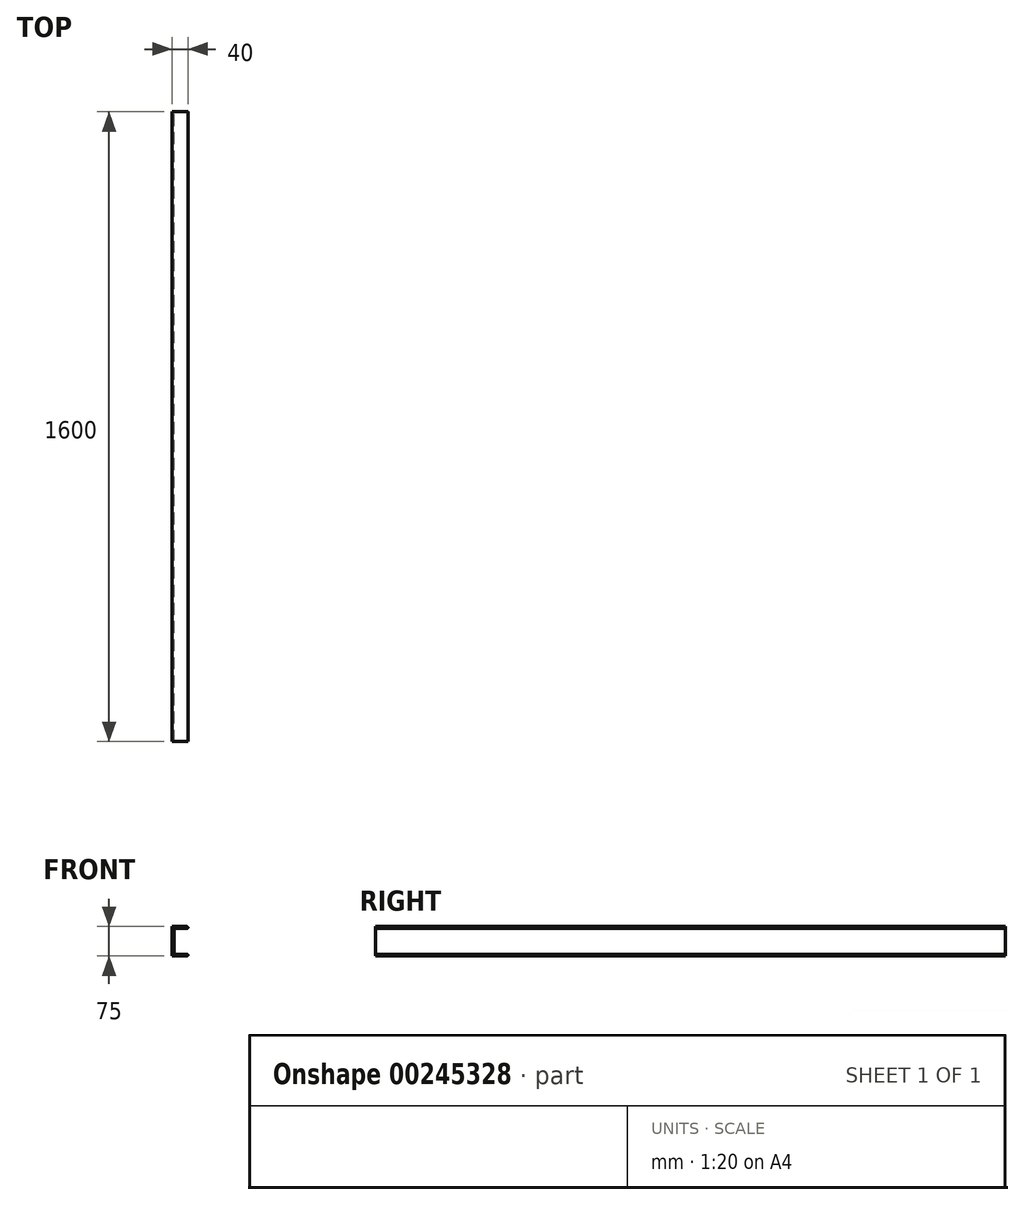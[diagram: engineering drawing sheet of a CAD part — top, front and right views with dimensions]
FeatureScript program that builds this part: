
annotation { "Feature Type Name" : "Feature", "Feature Type Description" : "" }
export const myFeature = defineFeature(function(context is Context, id is Id, definition is map)
    precondition{}
    {
        {
            var Q0;
            Q0=qCreatedBy(makeId("Front.planeOp"),FACE);
            var sketch = newSketch(context, id + "F0", { "sketchPlane" : qUnion([Q0])});
            skLineSegment(sketch, "E0", {"start": v(0, 0) * mm, "end": v(37.5, 0) * mm});
            skLineSegment(sketch, "E1", {"start": v(40, 2.5) * mm, "end": v(40, 2.5) * mm});
            skLineSegment(sketch, "E2", {"start": v(37.5, 5) * mm, "end": v(5, 5) * mm});
            skLineSegment(sketch, "E3", {"start": v(5, 5) * mm, "end": v(5, 70) * mm});
            skLineSegment(sketch, "E4", {"start": v(5, 70) * mm, "end": v(37.5, 70) * mm});
            skLineSegment(sketch, "E5", {"start": v(40, 72.5) * mm, "end": v(40, 72.5) * mm});
            skLineSegment(sketch, "E6", {"start": v(37.5, 75) * mm, "end": v(0, 75) * mm});
            skLineSegment(sketch, "E7", {"start": v(0, 75) * mm, "end": v(0, 0) * mm});
            skPoint(sketch, "E8.visualSharp", {"position": v(40, 75) * mm});
            skArc(sketch, "E8.filletArc", {"start": v(40, 72.5) * mm, "mid": v(39.27, 74.27) * mm, "end": v(37.5, 75) * mm});
            skPoint(sketch, "E9.visualSharp", {"position": v(40, 70) * mm});
            skArc(sketch, "E9.filletArc", {"start": v(37.5, 70) * mm, "mid": v(39.27, 70.73) * mm, "end": v(40, 72.5) * mm});
            skPoint(sketch, "E10.visualSharp", {"position": v(40, 5) * mm});
            skArc(sketch, "E10.filletArc", {"start": v(40, 2.5) * mm, "mid": v(39.27, 4.27) * mm, "end": v(37.5, 5) * mm});
            skPoint(sketch, "E11.visualSharp", {"position": v(40, 0) * mm});
            skArc(sketch, "E11.filletArc", {"start": v(37.5, 0) * mm, "mid": v(39.27, 0.73) * mm, "end": v(40, 2.5) * mm});
            skSolve(sketch);
        }
        {
            var Q0;
            Q0=qSketchRegion(id+"F0",true);
            extrude(context, id + "F1", {"entities" : qUnion([Q0]), "depth" : 1600 * mm});
        }
    });
